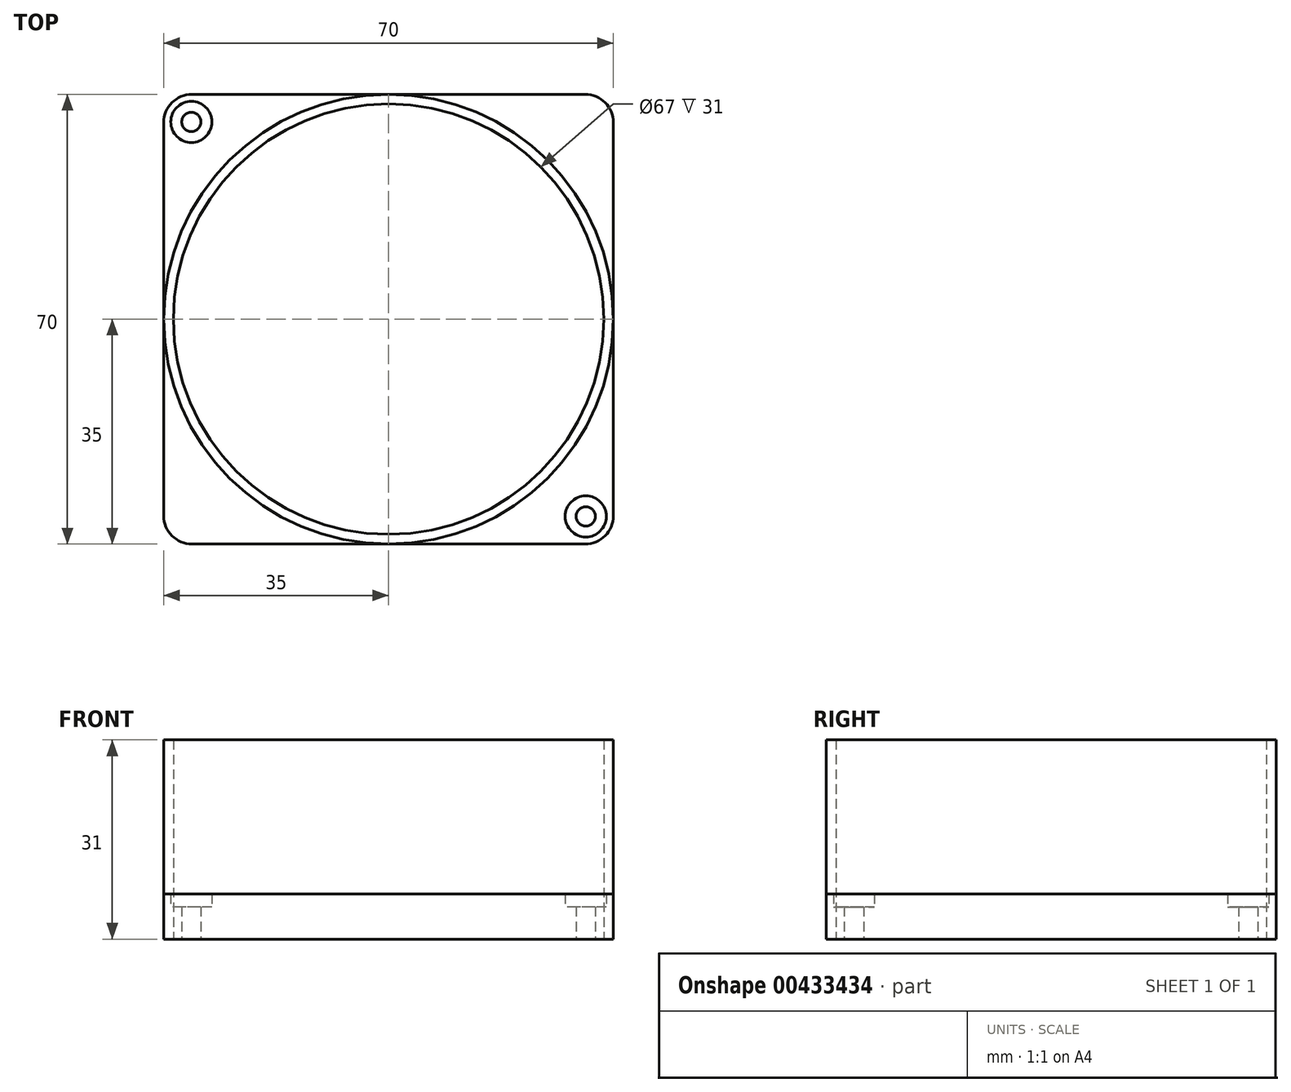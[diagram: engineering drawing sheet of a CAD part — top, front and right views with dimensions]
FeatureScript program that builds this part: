
annotation { "Feature Type Name" : "Feature", "Feature Type Description" : "" }
export const myFeature = defineFeature(function(context is Context, id is Id, definition is map)
    precondition{}
    {
        {
            var Q0;
            Q0=qCreatedBy(makeId("Top.planeOp"),FACE);
            var sketch = newSketch(context, id + "F0", { "sketchPlane" : qUnion([Q0])});
            skLineSegment(sketch, "E0.bottom", {"start": v(35, 35) * mm, "end": v(-35, 35) * mm});
            skLineSegment(sketch, "E0.top", {"start": v(35, -35) * mm, "end": v(-35, -35) * mm});
            skLineSegment(sketch, "E0.left", {"start": v(35, 35) * mm, "end": v(35, -35) * mm});
            skLineSegment(sketch, "E0.right", {"start": v(-35, 35) * mm, "end": v(-35, -35) * mm});
            skPoint(sketch, "E0.middle", {"position": v(0, 0) * mm});
            skCircle(sketch, "E1", {"center": v(0, 0) * mm, "radius": 35 * mm});
            skCircle(sketch, "E2", {"center": v(0, 0) * mm, "radius": 33.5 * mm});
            skCircle(sketch, "E3", {"center": v(-30.7, 30.7) * mm, "radius": 3.2 * mm});
            skCircle(sketch, "E4", {"center": v(30.7, -30.7) * mm, "radius": 3.2 * mm});
            skCircle(sketch, "E5", {"center": v(-30.7, 30.7) * mm, "radius": 1.5 * mm});
            skCircle(sketch, "E6", {"center": v(30.7, -30.7) * mm, "radius": 1.5 * mm});
            skSolve(sketch);
        }
        {
            var Q0;
            Q0=makeQuery(id+"F0.imprint","IMPRINT",FACE,{"disambiguationData":[TD([[makeQuery(id+"F0.imprint","IMPRINT",EDGE,{"derivedFrom":sQuery(id+"F0.wireOp",EDGE,"E2")}),-1.0]])]});
            extrude(context, id + "F1", {"entities" : qUnion([Q0]), "depth" : 31 * mm});
        }
        {
            var Q0;
            Q0 = qSketchRegion(id + "F0", true);
            extrude(context, id + "F2", {"entities" : qUnion([Q0]), "operationType" : NewBodyOperationType.ADD, "depth" : 7 * mm});
        }
        {
            var Q0;
            Q0=makeQuery(id+"F0.imprint","IMPRINT",FACE,{"disambiguationData":[TD([[makeQuery(id+"F0.imprint","IMPRINT",EDGE,{"derivedFrom":sQuery(id+"F0.wireOp",EDGE,"E3")}),1.0]])]});
            var Q1;
            Q1=makeQuery(id+"F0.imprint","IMPRINT",FACE,{"disambiguationData":[TD([[makeQuery(id+"F0.imprint","IMPRINT",EDGE,{"derivedFrom":sQuery(id+"F0.wireOp",EDGE,"E4")}),1.0]])]});
            extrude(context, id + "F3", {"entities" : qUnion([Q0, Q1]), "operationType" : NewBodyOperationType.ADD, "depth" : 5 * mm});
        }
        {
            var Q0;
            Q0=makeQuery(id+"F2.opExtrude","SWEPT_EDGE",EDGE,{"disambiguationData":[OSD([sQuery(id+"F0.wireOp",EDGE,"E0.bottom"),sQuery(id+"F0.wireOp",EDGE,"E0.right")])]});
            var Q1;
            Q1=makeQuery(id+"F2.opExtrude","SWEPT_EDGE",EDGE,{"disambiguationData":[OSD([sQuery(id+"F0.wireOp",EDGE,"E0.top"),sQuery(id+"F0.wireOp",EDGE,"E0.left")])]});
            var Q2;
            Q2=makeQuery(id+"F2.opExtrude","SWEPT_EDGE",EDGE,{"disambiguationData":[OSD([sQuery(id+"F0.wireOp",EDGE,"E0.bottom"),sQuery(id+"F0.wireOp",EDGE,"E0.left")])]});
            var Q3;
            Q3=makeQuery(id+"F2.opExtrude","SWEPT_EDGE",EDGE,{"disambiguationData":[OSD([sQuery(id+"F0.wireOp",EDGE,"E0.top"),sQuery(id+"F0.wireOp",EDGE,"E0.right")])]});
            fillet(context, id + "F4", {"entities" : qUnion([Q0, Q1, Q2, Q3]), "radius" : 4.4 * mm, "tangentPropagation" : true, "allowEdgeOverflow" : false});
        }
    });
